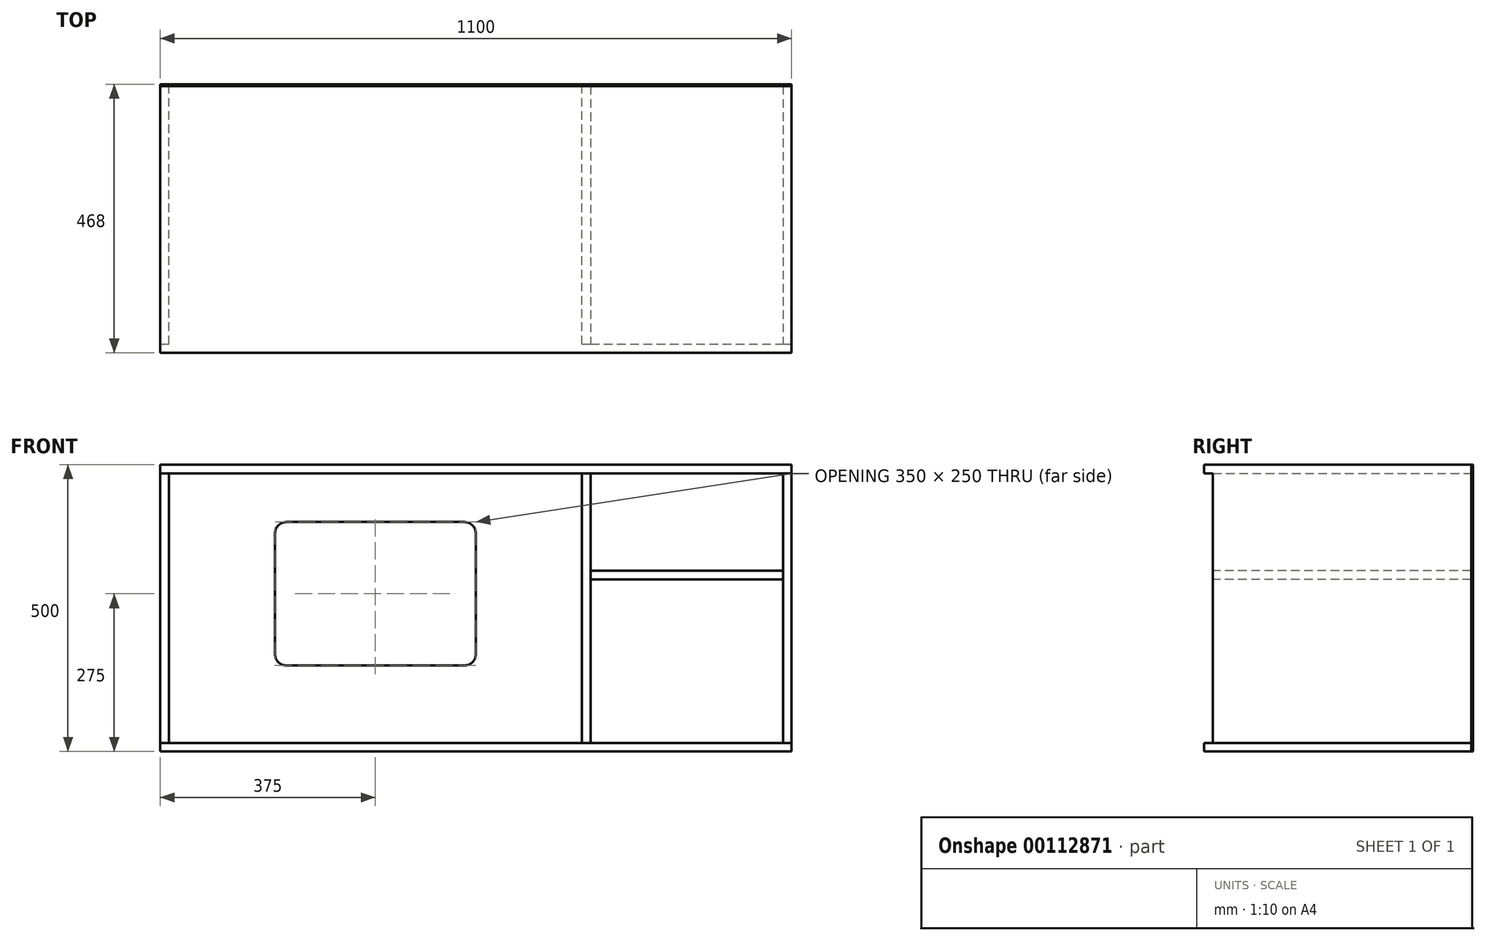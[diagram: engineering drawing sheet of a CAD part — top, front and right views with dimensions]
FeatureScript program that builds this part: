
annotation { "Feature Type Name" : "Feature", "Feature Type Description" : "" }
export const myFeature = defineFeature(function(context is Context, id is Id, definition is map)
    precondition{}
    {
        {
            var Q0;
            Q0=qCreatedBy(makeId("Top.planeOp"),FACE);
            var sketch = newSketch(context, id + "F0", { "sketchPlane" : qUnion([Q0])});
            skLineSegment(sketch, "E0.bottom", {"start": v(0, 0) * mm, "end": v(1100, 0) * mm});
            skLineSegment(sketch, "E0.top", {"start": v(0, 450) * mm, "end": v(1100, 450) * mm});
            skLineSegment(sketch, "E0.left", {"start": v(0, 0) * mm, "end": v(0, 450) * mm});
            skLineSegment(sketch, "E0.right", {"start": v(1100, 0) * mm, "end": v(1100, 450) * mm});
            skSolve(sketch);
        }
        {
            var Q0;
            Q0 = qSketchRegion(id + "F0", true);
            extrude(context, id + "F1", {"entities" : qUnion([Q0]), "depth" : 15 * mm});
        }
        {
            var Q0;
            Q0=makeQuery(id+"F1.opExtrude","CAP_FACE",FACE,{"disambiguationData":[OSD([sQuery(id+"F0.wireOp",EDGE,"E0.bottom"),sQuery(id+"F0.wireOp",EDGE,"E0.top"),sQuery(id+"F0.wireOp",EDGE,"E0.left"),sQuery(id+"F0.wireOp",EDGE,"E0.right")])],"isStart":true});
            var sketch = newSketch(context, id + "F2", { "sketchPlane" : qUnion([Q0])});
            skPoint(sketch, "E1.oppositeSnap0", {"position": v(550, -450) * mm});
            skLineSegment(sketch, "E2.bottom", {"start": v(1100, 0) * mm, "end": v(1085, 0) * mm});
            skLineSegment(sketch, "E2.top", {"start": v(1100, -450) * mm, "end": v(1085, -450) * mm});
            skLineSegment(sketch, "E2.left", {"start": v(1100, 0) * mm, "end": v(1100, -450) * mm});
            skLineSegment(sketch, "E2.right", {"start": v(1085, 0) * mm, "end": v(1085, -450) * mm});
            skLineSegment(sketch, "E3.bottom", {"start": v(0, 0) * mm, "end": v(15, 0) * mm});
            skLineSegment(sketch, "E3.top", {"start": v(0, -450) * mm, "end": v(15, -450) * mm});
            skLineSegment(sketch, "E3.left", {"start": v(0, 0) * mm, "end": v(0, -450) * mm});
            skLineSegment(sketch, "E3.right", {"start": v(15, 0) * mm, "end": v(15, -450) * mm});
            skLineSegment(sketch, "E4.bottom", {"start": v(750, 0) * mm, "end": v(735, 0) * mm});
            skLineSegment(sketch, "E4.top", {"start": v(750, -450) * mm, "end": v(735, -450) * mm});
            skLineSegment(sketch, "E4.left", {"start": v(750, 0) * mm, "end": v(750, -450) * mm});
            skLineSegment(sketch, "E4.right", {"start": v(735, 0) * mm, "end": v(735, -450) * mm});
            skSolve(sketch);
        }
        {
            var Q0;
            Q0 = qSketchRegion(id + "F2", true);
            extrude(context, id + "F3", {"entities" : qUnion([Q0]), "depth" : 470 * mm});
        }
        {
            var Q0;
            Q0=makeQuery(id+"F3.boolean.opBoolean","MERGE",FACE,{"derivedFrom":[makeQuery(id+"F1.opExtrude","SWEPT_FACE",FACE,{"disambiguationData":[OSD([sQuery(id+"F0.wireOp",EDGE,"E0.bottom")])]}),makeQuery(id+"F3.opExtrude","SWEPT_FACE",FACE,{"disambiguationData":[OSD([sQuery(id+"F2.wireOp",EDGE,"E2.bottom")])]}),makeQuery(id+"F3.opExtrude","SWEPT_FACE",FACE,{"disambiguationData":[OSD([sQuery(id+"F2.wireOp",EDGE,"E3.bottom")])]}),makeQuery(id+"F3.opExtrude","SWEPT_FACE",FACE,{"disambiguationData":[OSD([sQuery(id+"F2.wireOp",EDGE,"E4.bottom")])]})]});
            var sketch = newSketch(context, id + "F4", { "sketchPlane" : qUnion([Q0])});
            skLineSegment(sketch, "E5.bottom", {"start": v(1100, 15) * mm, "end": v(0, 15) * mm});
            skLineSegment(sketch, "E5.top", {"start": v(1100, 0) * mm, "end": v(0, 0) * mm});
            skLineSegment(sketch, "E5.left", {"start": v(1100, 15) * mm, "end": v(1100, 0) * mm});
            skLineSegment(sketch, "E5.right", {"start": v(0, 15) * mm, "end": v(0, 0) * mm});
            skSolve(sketch);
        }
        {
            var Q0;
            Q0 = qSketchRegion(id + "F4", true);
            extrude(context, id + "F5", {"entities" : qUnion([Q0]), "operationType" : NewBodyOperationType.ADD, "depth" : 15 * mm});
        }
        {
            var Q0;
            Q0=makeQuery(id+"F3.opExtrude","CAP_FACE",FACE,{"disambiguationData":[OSD([sQuery(id+"F2.wireOp",EDGE,"E3.bottom"),sQuery(id+"F2.wireOp",EDGE,"E3.top"),sQuery(id+"F2.wireOp",EDGE,"E3.left"),sQuery(id+"F2.wireOp",EDGE,"E3.right")])],"isStart":false});
            var sketch = newSketch(context, id + "F6", { "sketchPlane" : qUnion([Q0])});
            skLineSegment(sketch, "E6.bottom", {"start": v(0, -450) * mm, "end": v(1100, -450) * mm});
            skLineSegment(sketch, "E6.top", {"start": v(0, 15) * mm, "end": v(1100, 15) * mm});
            skLineSegment(sketch, "E6.left", {"start": v(0, -450) * mm, "end": v(0, 15) * mm});
            skLineSegment(sketch, "E6.right", {"start": v(1100, -450) * mm, "end": v(1100, 15) * mm});
            skSolve(sketch);
        }
        {
            var Q0;
            Q0 = qSketchRegion(id + "F6", true);
            extrude(context, id + "F7", {"entities" : qUnion([Q0]), "depth" : 15 * mm});
        }
        {
            var Q0;
            Q0=makeQuery(id+"F3.opExtrude","SWEPT_FACE",FACE,{"disambiguationData":[OSD([sQuery(id+"F2.wireOp",EDGE,"E4.bottom")])]});
            var sketch = newSketch(context, id + "F8", { "sketchPlane" : qUnion([Q0])});
            skLineSegment(sketch, "E7.bottom", {"start": v(750, -170) * mm, "end": v(1085, -170) * mm});
            skLineSegment(sketch, "E7.top", {"start": v(750, -185) * mm, "end": v(1085, -185) * mm});
            skLineSegment(sketch, "E7.left", {"start": v(750, -170) * mm, "end": v(750, -185) * mm});
            skLineSegment(sketch, "E7.right", {"start": v(1085, -170) * mm, "end": v(1085, -185) * mm});
            skSolve(sketch);
        }
        {
            var Q0;
            Q0 = qSketchRegion(id + "F8", true);
            var Q1;
            Q1=makeQuery(id+"F3.opExtrude","SWEPT_FACE",FACE,{"disambiguationData":[OSD([sQuery(id+"F2.wireOp",EDGE,"E2.top")])]});
            extrude(context, id + "F9", {"entities" : qUnion([Q0]), "endBound" : BoundingType.UP_TO_SURFACE, "oppositeDirection" : true, "endBoundEntityFace" : qUnion([Q1]), "depth" : 450 * mm});
        }
        {
            var Q0;
            Q0=makeQuery(id+"F1.opExtrude","SWEPT_FACE",FACE,{"disambiguationData":[OSD([sQuery(id+"F0.wireOp",EDGE,"E0.top")])]});
            var sketch = newSketch(context, id + "F10", { "sketchPlane" : qUnion([Q0])});
            skLineSegment(sketch, "E8.bottom", {"start": v(-1100, 15) * mm, "end": v(0, 15) * mm});
            skLineSegment(sketch, "E8.top", {"start": v(-1100, -485) * mm, "end": v(0, -485) * mm});
            skLineSegment(sketch, "E8.left", {"start": v(-1100, 15) * mm, "end": v(-1100, -485) * mm});
            skLineSegment(sketch, "E8.right", {"start": v(0, 15) * mm, "end": v(0, -485) * mm});
            skLineSegment(sketch, "E9.bottom", {"start": v(-530, -85) * mm, "end": v(-220, -85) * mm});
            skLineSegment(sketch, "E9.top", {"start": v(-530, -335) * mm, "end": v(-220, -335) * mm});
            skLineSegment(sketch, "E9.left", {"start": v(-550, -105) * mm, "end": v(-550, -315) * mm});
            skLineSegment(sketch, "E9.right", {"start": v(-200, -105) * mm, "end": v(-200, -315) * mm});
            skPoint(sketch, "E10.visualSharp", {"position": v(-550, -85) * mm});
            skArc(sketch, "E10.filletArc", {"start": v(-530, -85) * mm, "mid": v(-544.14, -90.86) * mm, "end": v(-550, -105) * mm});
            skPoint(sketch, "E11.visualSharp", {"position": v(-550, -335) * mm});
            skArc(sketch, "E11.filletArc", {"start": v(-550, -315) * mm, "mid": v(-544.14, -329.14) * mm, "end": v(-530, -335) * mm});
            skPoint(sketch, "E12.visualSharp", {"position": v(-200, -85) * mm});
            skArc(sketch, "E12.filletArc", {"start": v(-200, -105) * mm, "mid": v(-205.86, -90.86) * mm, "end": v(-220, -85) * mm});
            skPoint(sketch, "E13.visualSharp", {"position": v(-200, -335) * mm});
            skArc(sketch, "E13.filletArc", {"start": v(-220, -335) * mm, "mid": v(-205.86, -329.14) * mm, "end": v(-200, -315) * mm});
            skSolve(sketch);
        }
        {
            var Q0;
            Q0 = qSketchRegion(id + "F10", true);
            extrude(context, id + "F11", {"entities" : qUnion([Q0]), "depth" : 3 * mm});
        }
    });
